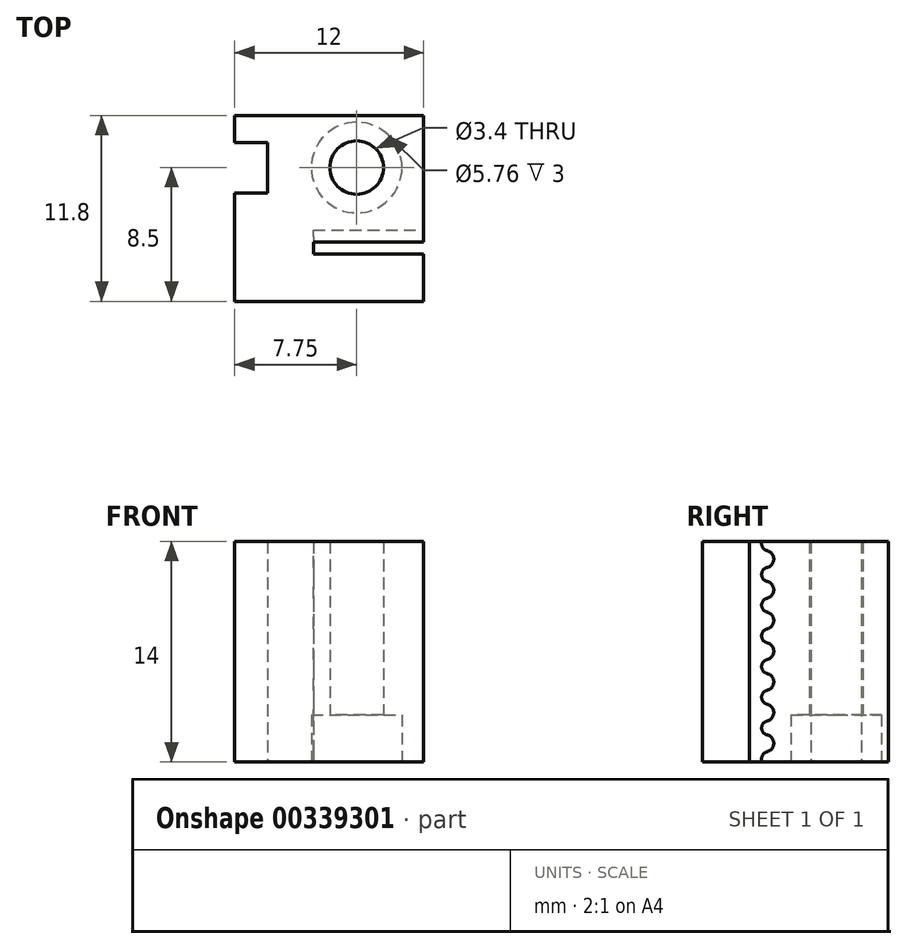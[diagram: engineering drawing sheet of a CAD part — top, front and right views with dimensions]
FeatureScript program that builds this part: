
annotation { "Feature Type Name" : "Feature", "Feature Type Description" : "" }
export const myFeature = defineFeature(function(context is Context, id is Id, definition is map)
    precondition{}
    {
        {
            var Q0;
            Q0=qCreatedBy(makeId("Top.planeOp"),FACE);
            var sketch = newSketch(context, id + "F0", { "sketchPlane" : qUnion([Q0])});
            skLineSegment(sketch, "E0.bottom", {"start": v(0, 0) * mm, "end": v(12, 0) * mm});
            skLineSegment(sketch, "E0.top", {"start": v(0, 11.8) * mm, "end": v(12, 11.8) * mm});
            skLineSegment(sketch, "E0.left", {"start": v(0, 0) * mm, "end": v(0, 11.8) * mm});
            skLineSegment(sketch, "E0.right", {"start": v(12, 0) * mm, "end": v(12, 11.8) * mm});
            skCircle(sketch, "E1", {"center": v(7.75, 8.5) * mm, "radius": 1.7 * mm});
            skLineSegment(sketch, "E2.bottom", {"start": v(0, 10.1) * mm, "end": v(2.1, 10.1) * mm});
            skLineSegment(sketch, "E2.top", {"start": v(0, 6.89) * mm, "end": v(2.1, 6.89) * mm});
            skLineSegment(sketch, "E2.left", {"start": v(0, 10.1) * mm, "end": v(0, 6.89) * mm});
            skLineSegment(sketch, "E2.right", {"start": v(2.1, 10.1) * mm, "end": v(2.1, 6.89) * mm});
            skLineSegment(sketch, "E3.bottom", {"start": v(12, 3.76) * mm, "end": v(5, 3.76) * mm});
            skLineSegment(sketch, "E3.top", {"start": v(12, 3) * mm, "end": v(5, 3) * mm});
            skLineSegment(sketch, "E3.left", {"start": v(12, 3.76) * mm, "end": v(12, 3) * mm});
            skLineSegment(sketch, "E3.right", {"start": v(5, 3.76) * mm, "end": v(5, 3) * mm});
            skSolve(sketch);
        }
        {
            var Q0;
            {var subQ6=sQuery(id+"F0.wireOp",EDGE,"E0.bottom");Q0=makeQuery(id+"F0.imprint","IMPRINT",FACE,{"disambiguationData":[TD([[makeQuery(id+"F0.imprint","IMPRINT",EDGE,{"derivedFrom":subQ6}),1.0]])]});}
            extrude(context, id + "F1", {"entities" : qUnion([Q0]), "depth" : 14 * mm});
        }
        {
            var Q0;
            Q0=makeQuery(id+"F1.opExtrude","CAP_FACE",FACE,{"disambiguationData":[OSD([sQuery(id+"F0.wireOp",EDGE,"E0.bottom"),sQuery(id+"F0.wireOp",EDGE,"E0.top"),sQuery(id+"F0.wireOp",EDGE,"E0.left"),sQuery(id+"F0.wireOp",EDGE,"E0.right"),sQuery(id+"F0.wireOp",EDGE,"E1"),sQuery(id+"F0.wireOp",EDGE,"E2.bottom"),sQuery(id+"F0.wireOp",EDGE,"E2.top"),sQuery(id+"F0.wireOp",EDGE,"E2.right"),sQuery(id+"F0.wireOp",EDGE,"E3.bottom"),sQuery(id+"F0.wireOp",EDGE,"E3.top"),sQuery(id+"F0.wireOp",EDGE,"E3.right")])],"isStart":true});
            var sketch = newSketch(context, id + "F2", { "sketchPlane" : qUnion([Q0])});
            skCircle(sketch, "E4", {"center": v(7.75, -8.5) * mm, "radius": 2.88 * mm});
            skSolve(sketch);
        }
        {
            var Q0;
            Q0=makeQuery(id+"F2.imprint","IMPRINT",FACE,{"disambiguationData":[TD([[makeQuery(id+"F2.imprint","IMPRINT",EDGE,{"derivedFrom":sQuery(id+"F2.wireOp",EDGE,"E4")}),1.0]])]});
            extrude(context, id + "F3", {"entities" : qUnion([Q0]), "operationType" : NewBodyOperationType.REMOVE, "oppositeDirection" : true, "depth" : 3 * mm});
        }
        {
            var Q0;
            {var subQ0=sQuery(id+"F0.wireOp",EDGE,"E0.right");Q0=makeQuery(id+"F1.opExtrude","SWEPT_FACE",FACE,{"disambiguationData":[OSD([subQ0]),TDD([makeQuery(id+"F0.imprint","IMPRINT",EDGE,{"disambiguationData":[TD([[makeQuery(id+"F0.imprint","INTERSECT",VERTEX,{"derivedFrom":[sQuery(id+"F0.wireOp",EDGE,"E0.top"),subQ0]}),1.0]])],"derivedFrom":subQ0})])]});}
            var sketch = newSketch(context, id + "F4", { "sketchPlane" : qUnion([Q0])});
            skLineSegment(sketch, "E5", {"start": v(3.98, 15.5) * mm, "end": v(3.98, -1.24) * mm, "construction": true});
            skCircle(sketch, "E6", {"center": v(3.98, 12.88) * mm, "radius": 0.55 * mm});
            skCircle(sketch, "E7.0.1.0", {"center": v(3.98, 10.93) * mm, "radius": 0.55 * mm});
            skCircle(sketch, "E7.0.2.0", {"center": v(3.98, 8.98) * mm, "radius": 0.55 * mm});
            skCircle(sketch, "E7.0.3.0", {"center": v(3.98, 7.03) * mm, "radius": 0.55 * mm});
            skCircle(sketch, "E7.0.4.0", {"center": v(3.98, 5.08) * mm, "radius": 0.55 * mm});
            skCircle(sketch, "E7.0.5.0", {"center": v(3.98, 3.13) * mm, "radius": 0.55 * mm});
            skCircle(sketch, "E7.0.6.0", {"center": v(3.98, 1.18) * mm, "radius": 0.55 * mm});
            skLineSegment(sketch, "E7.direction1", {"start": v(3.98, 12.88) * mm, "end": v(28.98, 12.88) * mm, "construction": true});
            skLineSegment(sketch, "E7.direction2", {"start": v(3.98, 12.88) * mm, "end": v(3.98, 10.93) * mm, "construction": true});
            skSolve(sketch);
        }
        {
            var Q0;
            Q0 = qSketchRegion(id + "F4", true);
            var Q1;
            Q1=makeQuery(id+"F1.opExtrude","SWEPT_FACE",FACE,{"disambiguationData":[OSD([sQuery(id+"F0.wireOp",EDGE,"E3.right")])]});
            extrude(context, id + "F5", {"entities" : qUnion([Q0]), "operationType" : NewBodyOperationType.REMOVE, "endBound" : BoundingType.UP_TO_SURFACE, "oppositeDirection" : true, "endBoundEntityFace" : qUnion([Q1]), "depth" : 7 * mm});
        }
        {
            var Q0;
            Q0=makeQuery(id+"F5.boolean.opBoolean","INTERSECT",EDGE,{"disambiguationData":[OD(0.0)],"derivedFrom":[makeQuery(id+"F1.opExtrude","SWEPT_FACE",FACE,{"disambiguationData":[OSD([sQuery(id+"F0.wireOp",EDGE,"E3.bottom")])]}),makeQuery(id+"F5.opExtrude","SWEPT_FACE",FACE,{"disambiguationData":[OSD([sQuery(id+"F4.wireOp",EDGE,"E6")])]})]});
            var Q1;
            Q1=makeQuery(id+"F5.boolean.opBoolean","INTERSECT",EDGE,{"disambiguationData":[OD(1.0)],"derivedFrom":[makeQuery(id+"F1.opExtrude","SWEPT_FACE",FACE,{"disambiguationData":[OSD([sQuery(id+"F0.wireOp",EDGE,"E3.bottom")])]}),makeQuery(id+"F5.opExtrude","SWEPT_FACE",FACE,{"disambiguationData":[OSD([sQuery(id+"F4.wireOp",EDGE,"E6")])]})]});
            var Q2;
            Q2=makeQuery(id+"F5.boolean.opBoolean","INTERSECT",EDGE,{"disambiguationData":[OD(0.0)],"derivedFrom":[makeQuery(id+"F1.opExtrude","SWEPT_FACE",FACE,{"disambiguationData":[OSD([sQuery(id+"F0.wireOp",EDGE,"E3.bottom")])]}),makeQuery(id+"F5.opExtrude","SWEPT_FACE",FACE,{"disambiguationData":[OSD([sQuery(id+"F4.wireOp",EDGE,"E7.0.1.0")])]})]});
            var Q3;
            Q3=makeQuery(id+"F5.boolean.opBoolean","INTERSECT",EDGE,{"disambiguationData":[OD(1.0)],"derivedFrom":[makeQuery(id+"F1.opExtrude","SWEPT_FACE",FACE,{"disambiguationData":[OSD([sQuery(id+"F0.wireOp",EDGE,"E3.bottom")])]}),makeQuery(id+"F5.opExtrude","SWEPT_FACE",FACE,{"disambiguationData":[OSD([sQuery(id+"F4.wireOp",EDGE,"E7.0.1.0")])]})]});
            var Q4;
            Q4=makeQuery(id+"F5.boolean.opBoolean","INTERSECT",EDGE,{"disambiguationData":[OD(0.0)],"derivedFrom":[makeQuery(id+"F1.opExtrude","SWEPT_FACE",FACE,{"disambiguationData":[OSD([sQuery(id+"F0.wireOp",EDGE,"E3.bottom")])]}),makeQuery(id+"F5.opExtrude","SWEPT_FACE",FACE,{"disambiguationData":[OSD([sQuery(id+"F4.wireOp",EDGE,"E7.0.2.0")])]})]});
            var Q5;
            Q5=makeQuery(id+"F5.boolean.opBoolean","INTERSECT",EDGE,{"disambiguationData":[OD(1.0)],"derivedFrom":[makeQuery(id+"F1.opExtrude","SWEPT_FACE",FACE,{"disambiguationData":[OSD([sQuery(id+"F0.wireOp",EDGE,"E3.bottom")])]}),makeQuery(id+"F5.opExtrude","SWEPT_FACE",FACE,{"disambiguationData":[OSD([sQuery(id+"F4.wireOp",EDGE,"E7.0.2.0")])]})]});
            var Q6;
            Q6=makeQuery(id+"F5.boolean.opBoolean","INTERSECT",EDGE,{"disambiguationData":[OD(0.0)],"derivedFrom":[makeQuery(id+"F1.opExtrude","SWEPT_FACE",FACE,{"disambiguationData":[OSD([sQuery(id+"F0.wireOp",EDGE,"E3.bottom")])]}),makeQuery(id+"F5.opExtrude","SWEPT_FACE",FACE,{"disambiguationData":[OSD([sQuery(id+"F4.wireOp",EDGE,"E7.0.3.0")])]})]});
            var Q7;
            Q7=makeQuery(id+"F5.boolean.opBoolean","INTERSECT",EDGE,{"disambiguationData":[OD(1.0)],"derivedFrom":[makeQuery(id+"F1.opExtrude","SWEPT_FACE",FACE,{"disambiguationData":[OSD([sQuery(id+"F0.wireOp",EDGE,"E3.bottom")])]}),makeQuery(id+"F5.opExtrude","SWEPT_FACE",FACE,{"disambiguationData":[OSD([sQuery(id+"F4.wireOp",EDGE,"E7.0.3.0")])]})]});
            var Q8;
            Q8=makeQuery(id+"F5.boolean.opBoolean","INTERSECT",EDGE,{"disambiguationData":[OD(0.0)],"derivedFrom":[makeQuery(id+"F1.opExtrude","SWEPT_FACE",FACE,{"disambiguationData":[OSD([sQuery(id+"F0.wireOp",EDGE,"E3.bottom")])]}),makeQuery(id+"F5.opExtrude","SWEPT_FACE",FACE,{"disambiguationData":[OSD([sQuery(id+"F4.wireOp",EDGE,"E7.0.4.0")])]})]});
            var Q9;
            Q9=makeQuery(id+"F5.boolean.opBoolean","INTERSECT",EDGE,{"disambiguationData":[OD(1.0)],"derivedFrom":[makeQuery(id+"F1.opExtrude","SWEPT_FACE",FACE,{"disambiguationData":[OSD([sQuery(id+"F0.wireOp",EDGE,"E3.bottom")])]}),makeQuery(id+"F5.opExtrude","SWEPT_FACE",FACE,{"disambiguationData":[OSD([sQuery(id+"F4.wireOp",EDGE,"E7.0.4.0")])]})]});
            var Q10;
            Q10=makeQuery(id+"F5.boolean.opBoolean","INTERSECT",EDGE,{"disambiguationData":[OD(0.0)],"derivedFrom":[makeQuery(id+"F1.opExtrude","SWEPT_FACE",FACE,{"disambiguationData":[OSD([sQuery(id+"F0.wireOp",EDGE,"E3.bottom")])]}),makeQuery(id+"F5.opExtrude","SWEPT_FACE",FACE,{"disambiguationData":[OSD([sQuery(id+"F4.wireOp",EDGE,"E7.0.5.0")])]})]});
            var Q11;
            Q11=makeQuery(id+"F5.boolean.opBoolean","INTERSECT",EDGE,{"disambiguationData":[OD(1.0)],"derivedFrom":[makeQuery(id+"F1.opExtrude","SWEPT_FACE",FACE,{"disambiguationData":[OSD([sQuery(id+"F0.wireOp",EDGE,"E3.bottom")])]}),makeQuery(id+"F5.opExtrude","SWEPT_FACE",FACE,{"disambiguationData":[OSD([sQuery(id+"F4.wireOp",EDGE,"E7.0.5.0")])]})]});
            var Q12;
            Q12=makeQuery(id+"F5.boolean.opBoolean","INTERSECT",EDGE,{"disambiguationData":[OD(1.0)],"derivedFrom":[makeQuery(id+"F1.opExtrude","SWEPT_FACE",FACE,{"disambiguationData":[OSD([sQuery(id+"F0.wireOp",EDGE,"E3.bottom")])]}),makeQuery(id+"F5.opExtrude","SWEPT_FACE",FACE,{"disambiguationData":[OSD([sQuery(id+"F4.wireOp",EDGE,"E7.0.6.0")])]})]});
            var Q13;
            Q13=makeQuery(id+"F5.boolean.opBoolean","INTERSECT",EDGE,{"disambiguationData":[OD(0.0)],"derivedFrom":[makeQuery(id+"F1.opExtrude","SWEPT_FACE",FACE,{"disambiguationData":[OSD([sQuery(id+"F0.wireOp",EDGE,"E3.bottom")])]}),makeQuery(id+"F5.opExtrude","SWEPT_FACE",FACE,{"disambiguationData":[OSD([sQuery(id+"F4.wireOp",EDGE,"E7.0.6.0")])]})]});
            fillet(context, id + "F6", {"entities" : qUnion([Q0, Q1, Q2, Q3, Q4, Q5, Q6, Q7, Q8, Q9, Q10, Q11, Q12, Q13]), "radius" : 0.45 * mm, "tangentPropagation" : true, "allowEdgeOverflow" : false});
        }
    });
